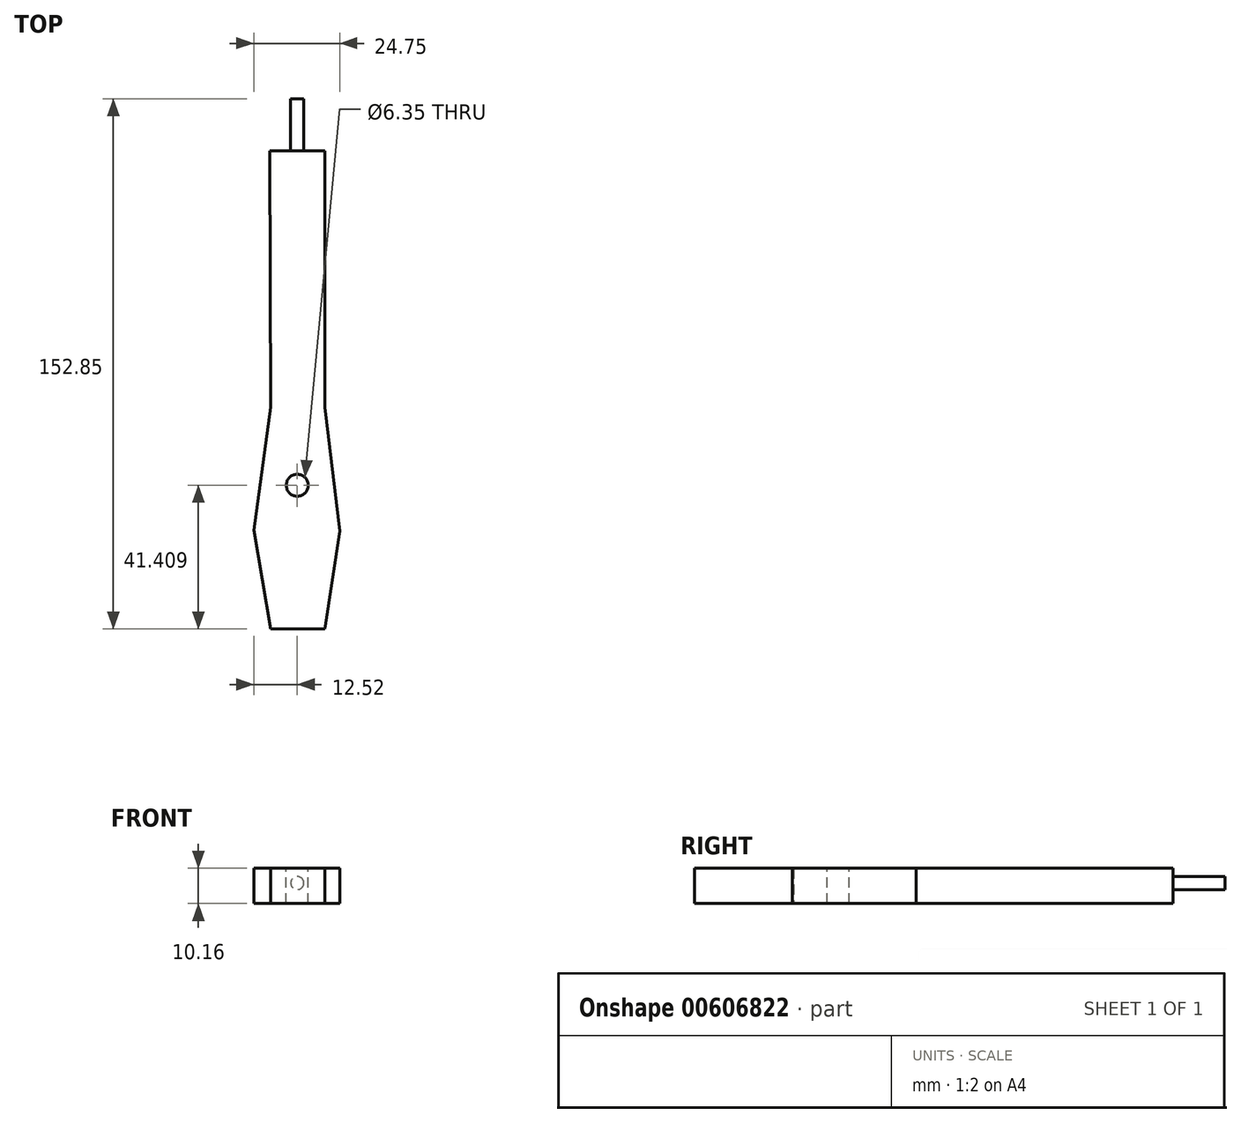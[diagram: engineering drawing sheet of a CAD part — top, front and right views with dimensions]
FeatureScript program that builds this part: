
annotation { "Feature Type Name" : "Feature", "Feature Type Description" : "" }
export const myFeature = defineFeature(function(context is Context, id is Id, definition is map)
    precondition{}
    {
        {
            var Q0;
            Q0=qCreatedBy(makeId("Top.planeOp"),FACE);
            var sketch = newSketch(context, id + "F0", { "sketchPlane" : qUnion([Q0])});
            skLineSegment(sketch, "E0", {"start": v(-7.91, 62.02) * mm, "end": v(7.91, 62.02) * mm});
            skLineSegment(sketch, "E1", {"start": v(7.91, 62.02) * mm, "end": v(7.91, -11.94) * mm});
            skLineSegment(sketch, "E2", {"start": v(7.91, -11.94) * mm, "end": v(12.23, -47.63) * mm});
            skLineSegment(sketch, "E3", {"start": v(12.23, -47.63) * mm, "end": v(7.91, -75.84) * mm});
            skLineSegment(sketch, "E4", {"start": v(7.91, -75.84) * mm, "end": v(-7.63, -75.84) * mm});
            skLineSegment(sketch, "E5", {"start": v(-7.63, -75.84) * mm, "end": v(-12.52, -47.34) * mm});
            skLineSegment(sketch, "E6", {"start": v(-12.52, -47.34) * mm, "end": v(-7.63, -11.94) * mm});
            skLineSegment(sketch, "E7", {"start": v(-7.63, -11.94) * mm, "end": v(-7.91, 62.02) * mm});
            skSolve(sketch);
        }
        {
            var Q0;
            Q0=makeQuery(id+"F0.imprint","IMPRINT",FACE,{"disambiguationData":[TD([[makeQuery(id+"F0.imprint","IMPRINT",EDGE,{"derivedFrom":sQuery(id+"F0.wireOp",EDGE,"E0")}),-1.0]])]});
            extrude(context, id + "F1", {"entities" : qUnion([Q0]), "depth" : 10.16 * mm, "offsetDistance" : 25.4 * mm});
        }
        {
            var Q0;
            Q0=makeQuery(id+"F1.opExtrude","SWEPT_FACE",FACE,{"disambiguationData":[OSD([sQuery(id+"F0.wireOp",EDGE,"E0")])]});
            var sketch = newSketch(context, id + "F2", { "sketchPlane" : qUnion([Q0])});
            skCircle(sketch, "E8", {"center": v(0, 5.9) * mm, "radius": 1.9 * mm});
            skSolve(sketch);
        }
        {
            var Q0;
            Q0=makeQuery(id+"F2.imprint","IMPRINT",FACE,{"disambiguationData":[TD([[makeQuery(id+"F2.imprint","IMPRINT",EDGE,{"derivedFrom":sQuery(id+"F2.wireOp",EDGE,"E8")}),1.0]])]});
            extrude(context, id + "F3", {"entities" : qUnion([Q0]), "operationType" : NewBodyOperationType.ADD, "depth" : 15 * mm, "offsetDistance" : 25.4 * mm});
        }
        {
            var Q0;
            Q0=makeQuery(id+"F1.opExtrude","CAP_FACE",FACE,{"disambiguationData":[OSD([sQuery(id+"F0.wireOp",EDGE,"E0"),sQuery(id+"F0.wireOp",EDGE,"E1"),sQuery(id+"F0.wireOp",EDGE,"E2"),sQuery(id+"F0.wireOp",EDGE,"E3"),sQuery(id+"F0.wireOp",EDGE,"E4"),sQuery(id+"F0.wireOp",EDGE,"E5"),sQuery(id+"F0.wireOp",EDGE,"E6"),sQuery(id+"F0.wireOp",EDGE,"E7")])],"isStart":false});
            var sketch = newSketch(context, id + "F4", { "sketchPlane" : qUnion([Q0])});
            skCircle(sketch, "E9", {"center": v(0, -34.43) * mm, "radius": 2.54 * mm});
            skSolve(sketch);
        }
        {
            var Q0;
            Q0=sQuery(id+"F4.wireOp",VERTEX,"E9.center");
            var Q1;
            Q1=makeQuery(id+"F1.opExtrude","SWEPT_BODY",BODY,{"disambiguationData":[OSD([sQuery(id+"F0.wireOp",EDGE,"E0"),sQuery(id+"F0.wireOp",EDGE,"E1"),sQuery(id+"F0.wireOp",EDGE,"E2"),sQuery(id+"F0.wireOp",EDGE,"E3"),sQuery(id+"F0.wireOp",EDGE,"E4"),sQuery(id+"F0.wireOp",EDGE,"E5"),sQuery(id+"F0.wireOp",EDGE,"E6"),sQuery(id+"F0.wireOp",EDGE,"E7")])]});
            hole(context, id + "F5", {"style" : HoleStyle.SIMPLE, "endStyle" : HoleEndStyle.THROUGH, "holeDiameter" : 6.35 * mm, "majorDiameter" : 6.35 * mm, "isTappedThrough" : true, "tappedDepth" : 12.7 * mm, "tapClearance" : 3, "locations" : qUnion([Q0]), "scope" : qUnion([Q1])});
        }
    });
